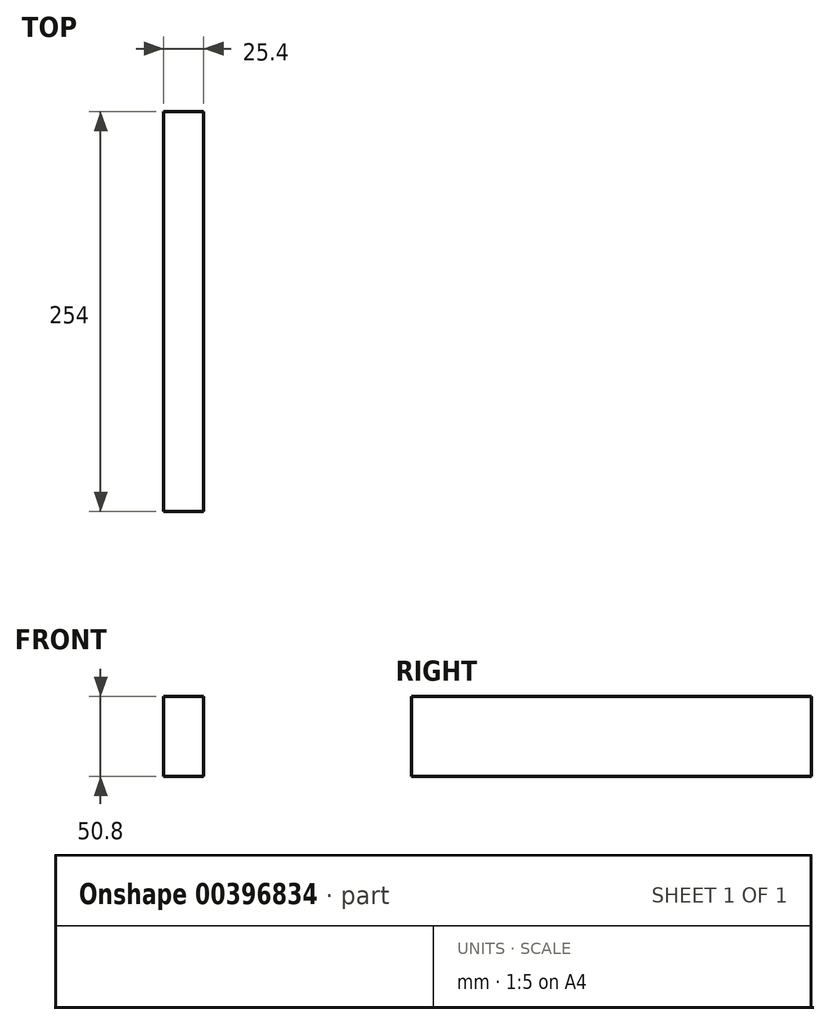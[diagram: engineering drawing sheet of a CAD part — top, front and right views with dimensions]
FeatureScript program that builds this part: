
annotation { "Feature Type Name" : "Feature", "Feature Type Description" : "" }
export const myFeature = defineFeature(function(context is Context, id is Id, definition is map)
    precondition{}
    {
        {
            var Q0;
            Q0=qCreatedBy(makeId("Right.planeOp"),FACE);
            var sketch = newSketch(context, id + "F0", { "sketchPlane" : qUnion([Q0])});
            skLineSegment(sketch, "E0.bottom", {"start": v(-127, 25.4) * mm, "end": v(127, 25.4) * mm});
            skLineSegment(sketch, "E0.top", {"start": v(-127, -25.4) * mm, "end": v(127, -25.4) * mm});
            skLineSegment(sketch, "E0.left", {"start": v(-127, 25.4) * mm, "end": v(-127, -25.4) * mm});
            skLineSegment(sketch, "E0.right", {"start": v(127, 25.4) * mm, "end": v(127, -25.4) * mm});
            skPoint(sketch, "E0.middle", {"position": v(0, 0) * mm});
            skSolve(sketch);
        }
        {
            var Q0;
            Q0=makeQuery(id+"F0.imprint","IMPRINT",FACE,{"disambiguationData":[TD([[makeQuery(id+"F0.imprint","IMPRINT",EDGE,{"derivedFrom":sQuery(id+"F0.wireOp",EDGE,"E0.bottom")}),-1.0]])]});
            extrude(context, id + "F1", {"entities" : qUnion([Q0]), "depth" : 25.4 * mm});
        }
    });
